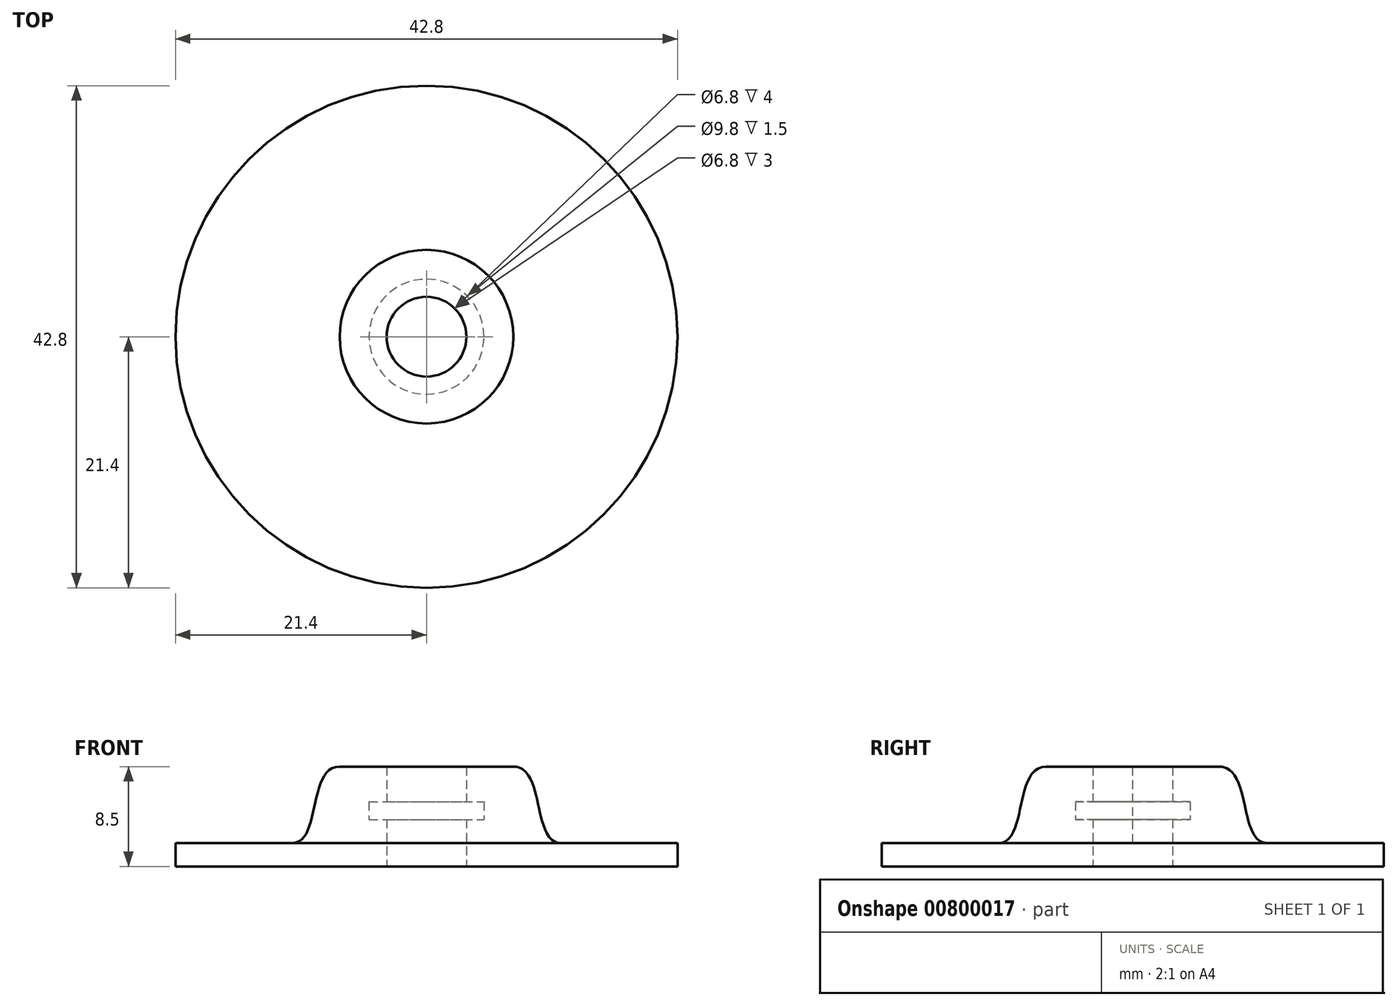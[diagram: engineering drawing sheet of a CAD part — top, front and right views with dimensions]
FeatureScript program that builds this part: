
annotation { "Feature Type Name" : "Feature", "Feature Type Description" : "" }
export const myFeature = defineFeature(function(context is Context, id is Id, definition is map)
    precondition{}
    {
        {
            var Q0;
            Q0=qCreatedBy(makeId("Front.planeOp"),FACE);
            var sketch = newSketch(context, id + "F0", { "sketchPlane" : qUnion([Q0])});
            skLineSegment(sketch, "E0.bottom", {"start": v(-3.4, 0) * mm, "end": v(-11.4, 0) * mm});
            skLineSegment(sketch, "E0.top", {"start": v(-3.4, 2) * mm, "end": v(-11.4, 2) * mm});
            skLineSegment(sketch, "E0.left", {"start": v(-3.4, 0) * mm, "end": v(-3.4, 2) * mm});
            skLineSegment(sketch, "E0.right", {"start": v(-11.4, 0) * mm, "end": v(-11.4, 2) * mm});
            skLineSegment(sketch, "E1.bottom", {"start": v(-3.4, 2) * mm, "end": v(-7.4, 2) * mm});
            skLineSegment(sketch, "E1.top", {"start": v(-3.4, 4) * mm, "end": v(-7.4, 4) * mm});
            skLineSegment(sketch, "E1.left", {"start": v(-3.4, 2) * mm, "end": v(-3.4, 4) * mm});
            skLineSegment(sketch, "E1.right", {"start": v(-7.4, 2) * mm, "end": v(-7.4, 4) * mm});
            skLineSegment(sketch, "E2.bottom", {"start": v(-7.4, 4) * mm, "end": v(-4.9, 4) * mm});
            skLineSegment(sketch, "E2.top", {"start": v(-7.4, 5.5) * mm, "end": v(-4.9, 5.5) * mm});
            skLineSegment(sketch, "E2.left", {"start": v(-7.4, 4) * mm, "end": v(-7.4, 5.5) * mm});
            skLineSegment(sketch, "E2.right", {"start": v(-4.9, 4) * mm, "end": v(-4.9, 5.5) * mm});
            skLineSegment(sketch, "E3.bottom", {"start": v(-7.4, 5.5) * mm, "end": v(-3.4, 5.5) * mm});
            skLineSegment(sketch, "E3.top", {"start": v(-7.4, 8.5) * mm, "end": v(-3.4, 8.5) * mm});
            skLineSegment(sketch, "E3.left", {"start": v(-7.4, 5.5) * mm, "end": v(-7.4, 8.5) * mm});
            skLineSegment(sketch, "E3.right", {"start": v(-3.4, 5.5) * mm, "end": v(-3.4, 8.5) * mm});
            skPoint(sketch, "E4.oppositeSnap0", {"position": v(-5.4, 8.5) * mm});
            skLineSegment(sketch, "E4.bottom", {"start": v(-3.4, 8.5) * mm, "end": v(-5.4, 8.5) * mm});
            skLineSegment(sketch, "E5.bottom", {"start": v(-11.4, 0) * mm, "end": v(-21.4, 0) * mm});
            skLineSegment(sketch, "E5.top", {"start": v(-11.4, 2) * mm, "end": v(-21.4, 2) * mm});
            skLineSegment(sketch, "E5.right", {"start": v(-21.4, 0) * mm, "end": v(-21.4, 2) * mm});
            skFitSpline(sketch, "E6", {"points": [v(-11.4, 2) * mm, v(-7.4, 8.5) * mm], "startDerivative": vector(7.2, 0) * mm, "endDerivative": vector(8.2, -0.09) * mm});
            skPoint(sketch, "E7", {"position": v(0, 6.8) * mm});
            skLineSegment(sketch, "E8", {"start": v(0, 0) * mm, "end": v(0, 6.8) * mm});
            skSolve(sketch);
        }
        {
            var Q0;
            Q0 = qSketchRegion(id + "F0", true);
            var Q1;
            Q1=sQuery(id+"F0.wireOp",EDGE,"E8");
            revolve(context, id + "F1", {"surfaceOperationType" : NewSurfaceOperationType.NEW, "entities" : qUnion([Q0]), "axis" : qUnion([Q1]), "revolveType" : RevolveType.FULL});
        }
    });
